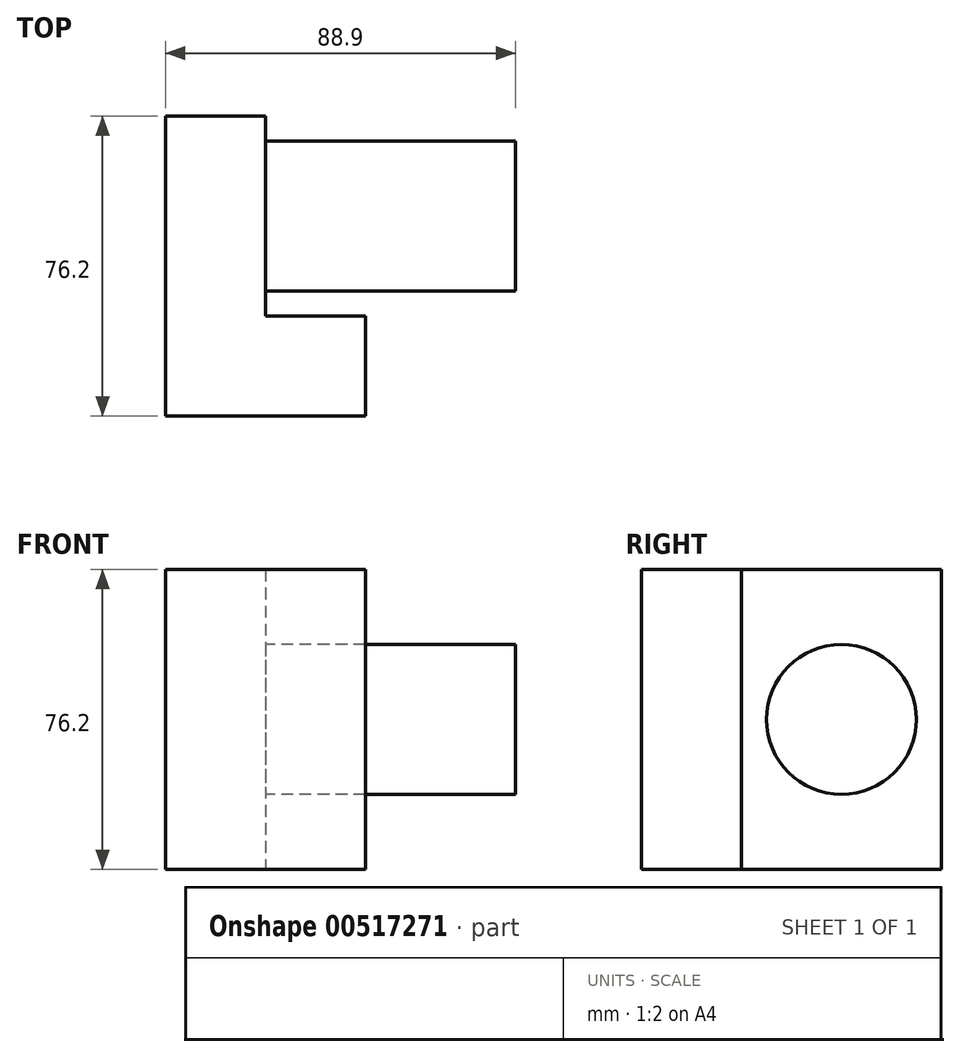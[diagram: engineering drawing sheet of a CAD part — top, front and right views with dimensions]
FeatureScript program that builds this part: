
annotation { "Feature Type Name" : "Feature", "Feature Type Description" : "" }
export const myFeature = defineFeature(function(context is Context, id is Id, definition is map)
    precondition{}
    {
        {
            var Q0;
            Q0=qCreatedBy(makeId("Top.planeOp"),FACE);
            var sketch = newSketch(context, id + "F0", { "sketchPlane" : qUnion([Q0])});
            skLineSegment(sketch, "E0", {"start": v(-40.58, 22.98) * mm, "end": v(-40.58, -53.22) * mm});
            skLineSegment(sketch, "E1", {"start": v(-40.58, -53.22) * mm, "end": v(10.22, -53.22) * mm});
            skLineSegment(sketch, "E2", {"start": v(10.22, -53.22) * mm, "end": v(10.22, -27.82) * mm});
            skLineSegment(sketch, "E3", {"start": v(10.22, -27.82) * mm, "end": v(-15.18, -27.82) * mm});
            skLineSegment(sketch, "E4", {"start": v(-15.18, -27.82) * mm, "end": v(-15.18, 22.98) * mm});
            skLineSegment(sketch, "E5", {"start": v(-40.58, 22.98) * mm, "end": v(-15.18, 22.98) * mm});
            skSolve(sketch);
        }
        {
            var Q0;
            Q0 = qSketchRegion(id + "F0", true);
            extrude(context, id + "F1", {"entities" : qUnion([Q0]), "depth" : 76.2 * mm, "offsetDistance" : 25.4 * mm});
        }
        {
            var Q0;
            Q0=makeQuery(id+"F1.opExtrude","SWEPT_FACE",FACE,{"disambiguationData":[OSD([sQuery(id+"F0.wireOp",EDGE,"E4")])]});
            var sketch = newSketch(context, id + "F2", { "sketchPlane" : qUnion([Q0])});
            skLineSegment(sketch, "E6", {"start": v(-27.82, 38.1) * mm, "end": v(-2.42, 38.1) * mm});
            skCircle(sketch, "E7", {"center": v(-2.42, 38.1) * mm, "radius": 19.05 * mm});
            skSolve(sketch);
        }
        {
            var Q0;
            Q0 = qSketchRegion(id + "F2", true);
            extrude(context, id + "F3", {"entities" : qUnion([Q0]), "operationType" : NewBodyOperationType.ADD, "depth" : 63.5 * mm, "offsetDistance" : 25.4 * mm});
        }
    });
